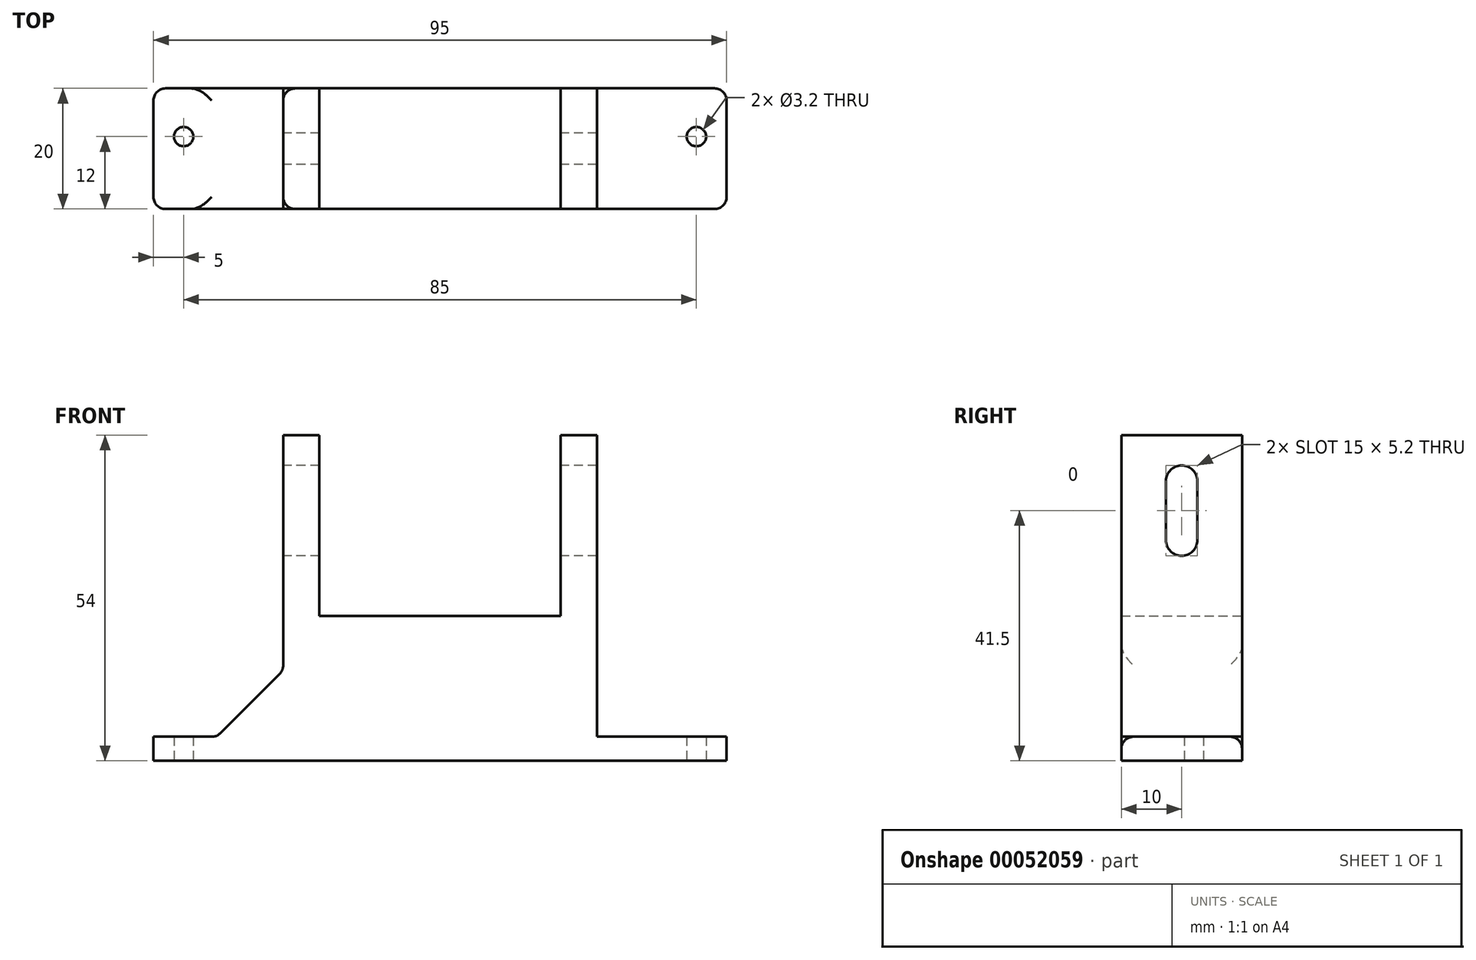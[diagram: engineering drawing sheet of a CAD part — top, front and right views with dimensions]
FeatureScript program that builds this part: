
annotation { "Feature Type Name" : "Feature", "Feature Type Description" : "" }
export const myFeature = defineFeature(function(context is Context, id is Id, definition is map)
    precondition{}
    {
        {
            var Q0;
            Q0=qCreatedBy(makeId("Top.planeOp"),FACE);
            var sketch = newSketch(context, id + "F0", { "sketchPlane" : qUnion([Q0])});
            skLineSegment(sketch, "E0.bottom", {"start": v(-47.5, 8) * mm, "end": v(47.5, 8) * mm});
            skLineSegment(sketch, "E0.top", {"start": v(-47.5, -12) * mm, "end": v(47.5, -12) * mm});
            skLineSegment(sketch, "E0.left", {"start": v(-47.5, 8) * mm, "end": v(-47.5, -12) * mm});
            skLineSegment(sketch, "E0.right", {"start": v(47.5, 8) * mm, "end": v(47.5, -12) * mm});
            skCircle(sketch, "E1", {"center": v(-42.5, 0) * mm, "radius": 1.6 * mm});
            skCircle(sketch, "E2", {"center": v(42.5, 0) * mm, "radius": 1.6 * mm});
            skSolve(sketch);
        }
        {
            var Q0;
            Q0=makeQuery(id+"F0.imprint","IMPRINT",FACE,{"disambiguationData":[TD([[makeQuery(id+"F0.imprint","IMPRINT",EDGE,{"derivedFrom":sQuery(id+"F0.wireOp",EDGE,"E0.bottom")}),-1.0]])]});
            extrude(context, id + "F1", {"entities" : qUnion([Q0]), "depth" : 4 * mm});
        }
        {
            var Q0;
            Q0=makeQuery(id+"F1.opExtrude","SWEPT_FACE",FACE,{"disambiguationData":[OSD([sQuery(id+"F0.wireOp",EDGE,"E0.bottom")])]});
            var sketch = newSketch(context, id + "F2", { "sketchPlane" : qUnion([Q0])});
            skLineSegment(sketch, "E3", {"start": v(-26, 4) * mm, "end": v(-26, 54) * mm});
            skLineSegment(sketch, "E4", {"start": v(-26, 54) * mm, "end": v(-20, 54) * mm});
            skLineSegment(sketch, "E5", {"start": v(-20, 54) * mm, "end": v(-20, 24) * mm});
            skLineSegment(sketch, "E6", {"start": v(-20, 24) * mm, "end": v(20, 24) * mm});
            skLineSegment(sketch, "E7", {"start": v(20, 24) * mm, "end": v(20, 54) * mm});
            skLineSegment(sketch, "E8", {"start": v(20, 54) * mm, "end": v(26, 54) * mm});
            skLineSegment(sketch, "E9", {"start": v(26, 54) * mm, "end": v(26, 4) * mm});
            skSolve(sketch);
        }
        {
            var Q0;
            {var subQ0=sQuery(id+"F2.wireOp",EDGE,"E3");Q0=makeQuery(id+"F2.imprint","IMPRINT",FACE,{"disambiguationData":[TD([[makeQuery(id+"F2.imprint","IMPRINT",EDGE,{"derivedFrom":subQ0}),-1.0]])]});}
            var Q1;
            Q1=makeQuery(id+"F1.opExtrude","SWEPT_FACE",FACE,{"disambiguationData":[OSD([sQuery(id+"F0.wireOp",EDGE,"E0.top")])]});
            extrude(context, id + "F3", {"entities" : qUnion([Q0]), "operationType" : NewBodyOperationType.ADD, "endBound" : BoundingType.UP_TO_SURFACE, "oppositeDirection" : true, "endBoundEntityFace" : qUnion([Q1]), "depth" : 25 * mm});
        }
        {
            var Q0;
            Q0=makeQuery(id+"F3.opExtrude","SWEPT_EDGE",EDGE,{"disambiguationData":[OSD([sQuery(id+"F0.wireOp",EDGE,"E0.bottom"),sQuery(id+"F2.wireOp",EDGE,"E3")])]});
            var Q1;
            Q1=makeQuery(id+"F3.opExtrude","SWEPT_EDGE",EDGE,{"disambiguationData":[OSD([sQuery(id+"F0.wireOp",EDGE,"E0.bottom"),sQuery(id+"F2.wireOp",EDGE,"E9")])]});
            chamfer(context, id + "F4", {"entities" : qUnion([Q0, Q1]), "width" : 11 * mm, "tangentPropagation" : true});
        }
        {
            var Q0;
            Q0=makeQuery(id+"F3.opExtrude","SWEPT_FACE",FACE,{"disambiguationData":[OSD([sQuery(id+"F2.wireOp",EDGE,"E9")])]});
            var sketch = newSketch(context, id + "F5", { "sketchPlane" : qUnion([Q0])});
            skLineSegment(sketch, "E10.bottom", {"start": v(2, 49) * mm, "end": v(2, 49) * mm});
            skLineSegment(sketch, "E10.top", {"start": v(2, 34) * mm, "end": v(2, 34) * mm});
            skLineSegment(sketch, "E10.left", {"start": v(-0.6, 46.4) * mm, "end": v(-0.6, 36.6) * mm});
            skLineSegment(sketch, "E10.right", {"start": v(4.6, 46.4) * mm, "end": v(4.6, 36.6) * mm});
            skPoint(sketch, "E11.visualSharp", {"position": v(-0.6, 49) * mm});
            skArc(sketch, "E11.filletArc", {"start": v(2, 49) * mm, "mid": v(0.16, 48.24) * mm, "end": v(-0.6, 46.4) * mm});
            skPoint(sketch, "E12.visualSharp", {"position": v(4.6, 49) * mm});
            skArc(sketch, "E12.filletArc", {"start": v(4.6, 46.4) * mm, "mid": v(3.84, 48.24) * mm, "end": v(2, 49) * mm});
            skPoint(sketch, "E13.visualSharp", {"position": v(4.6, 34) * mm});
            skArc(sketch, "E13.filletArc", {"start": v(2, 34) * mm, "mid": v(3.84, 34.76) * mm, "end": v(4.6, 36.6) * mm});
            skPoint(sketch, "E14.visualSharp", {"position": v(-0.6, 34) * mm});
            skArc(sketch, "E14.filletArc", {"start": v(-0.6, 36.6) * mm, "mid": v(0.16, 34.76) * mm, "end": v(2, 34) * mm});
            skSolve(sketch);
        }
        {
            var Q0;
            Q0=makeQuery(id+"F5.imprint","IMPRINT",FACE,{"disambiguationData":[TD([[makeQuery(id+"F5.imprint","IMPRINT",EDGE,{"derivedFrom":sQuery(id+"F5.wireOp",EDGE,"E10.left")}),1.0]])]});
            var Q1;
            Q1=makeQuery(id+"F3.opExtrude","SWEPT_FACE",FACE,{"disambiguationData":[OSD([sQuery(id+"F2.wireOp",EDGE,"E3")])]});
            extrude(context, id + "F6", {"entities" : qUnion([Q0]), "operationType" : NewBodyOperationType.REMOVE, "endBound" : BoundingType.UP_TO_SURFACE, "oppositeDirection" : true, "endBoundEntityFace" : qUnion([Q1]), "depth" : 25 * mm});
        }
        {
            var Q0;
            Q0=makeQuery(id+"F4.opChamfer","BLEND_FACE",FACE,{"disambiguationData":[OSD([sQuery(id+"F0.wireOp",EDGE,"E0.bottom"),sQuery(id+"F2.wireOp",EDGE,"E3")])]});
            var Q1;
            Q1=makeQuery(id+"F4.opChamfer","BLEND_FACE",FACE,{"disambiguationData":[OSD([sQuery(id+"F0.wireOp",EDGE,"E0.bottom"),sQuery(id+"F2.wireOp",EDGE,"E9")])]});
            var Q2;
            Q2=makeQuery(id+"F1.opExtrude","SWEPT_EDGE",EDGE,{"disambiguationData":[OSD([sQuery(id+"F0.wireOp",EDGE,"E0.top"),sQuery(id+"F0.wireOp",EDGE,"E0.left")])]});
            var Q3;
            Q3=makeQuery(id+"F1.opExtrude","SWEPT_EDGE",EDGE,{"disambiguationData":[OSD([sQuery(id+"F0.wireOp",EDGE,"E0.bottom"),sQuery(id+"F0.wireOp",EDGE,"E0.left")])]});
            var Q4;
            Q4=makeQuery(id+"F1.opExtrude","SWEPT_EDGE",EDGE,{"disambiguationData":[OSD([sQuery(id+"F0.wireOp",EDGE,"E0.top"),sQuery(id+"F0.wireOp",EDGE,"E0.right")])]});
            var Q5;
            Q5=makeQuery(id+"F1.opExtrude","SWEPT_EDGE",EDGE,{"disambiguationData":[OSD([sQuery(id+"F0.wireOp",EDGE,"E0.bottom"),sQuery(id+"F0.wireOp",EDGE,"E0.right")])]});
            fillet(context, id + "F7", {"entities" : qUnion([Q0, Q1, Q2, Q3, Q4, Q5]), "radius" : 2 * mm, "tangentPropagation" : true, "allowEdgeOverflow" : false});
        }
    });
